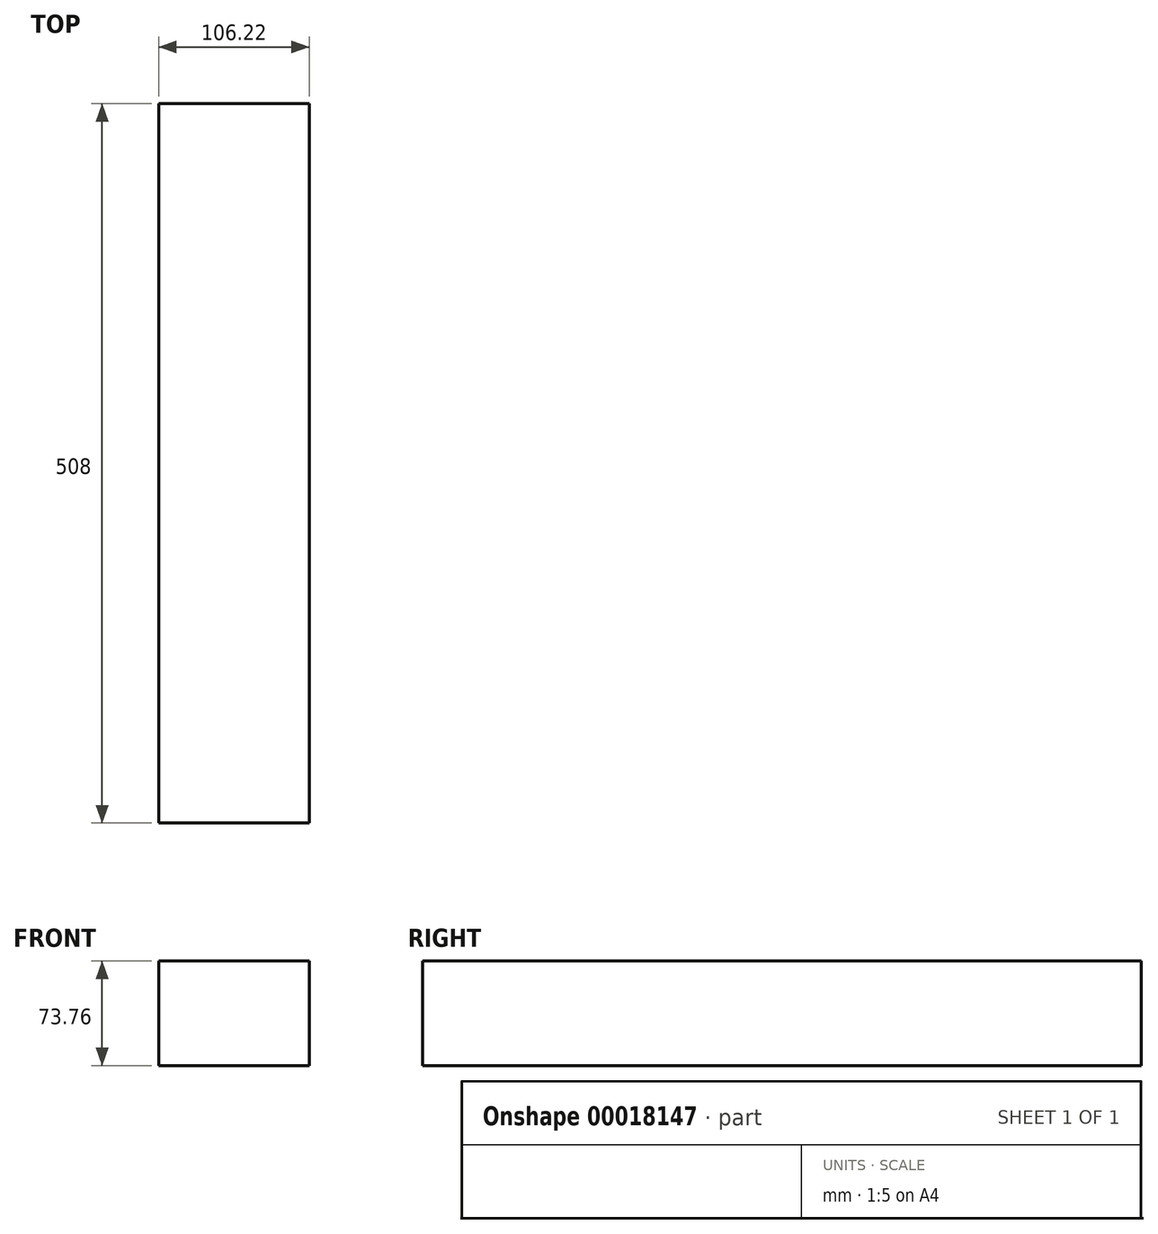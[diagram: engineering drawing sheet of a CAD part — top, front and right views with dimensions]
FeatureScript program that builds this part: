
annotation { "Feature Type Name" : "Feature", "Feature Type Description" : "" }
export const myFeature = defineFeature(function(context is Context, id is Id, definition is map)
    precondition{}
    {
        {
            var Q0;
            Q0=qCreatedBy(makeId("Front.planeOp"),FACE);
            var sketch = newSketch(context, id + "F0", { "sketchPlane" : qUnion([Q0])});
            skLineSegment(sketch, "E0.rect.bottom", {"start": v(53.1, -36.88) * mm, "end": v(-53.1, -36.88) * mm});
            skLineSegment(sketch, "E0.rect.top", {"start": v(53.1, 36.88) * mm, "end": v(-53.1, 36.88) * mm});
            skLineSegment(sketch, "E0.rect.left", {"start": v(53.1, -36.88) * mm, "end": v(53.1, 36.88) * mm});
            skLineSegment(sketch, "E0.rect.right", {"start": v(-53.1, -36.88) * mm, "end": v(-53.1, 36.88) * mm});
            skPoint(sketch, "E0.rect.middle", {"position": v(0, 0) * mm});
            skSolve(sketch);
        }
        {
            var Q0;
            Q0 = qSketchRegion(id + "F0", true);
            extrude(context, id + "F1", {"entities" : qUnion([Q0]), "depth" : 508 * mm});
        }
    });
